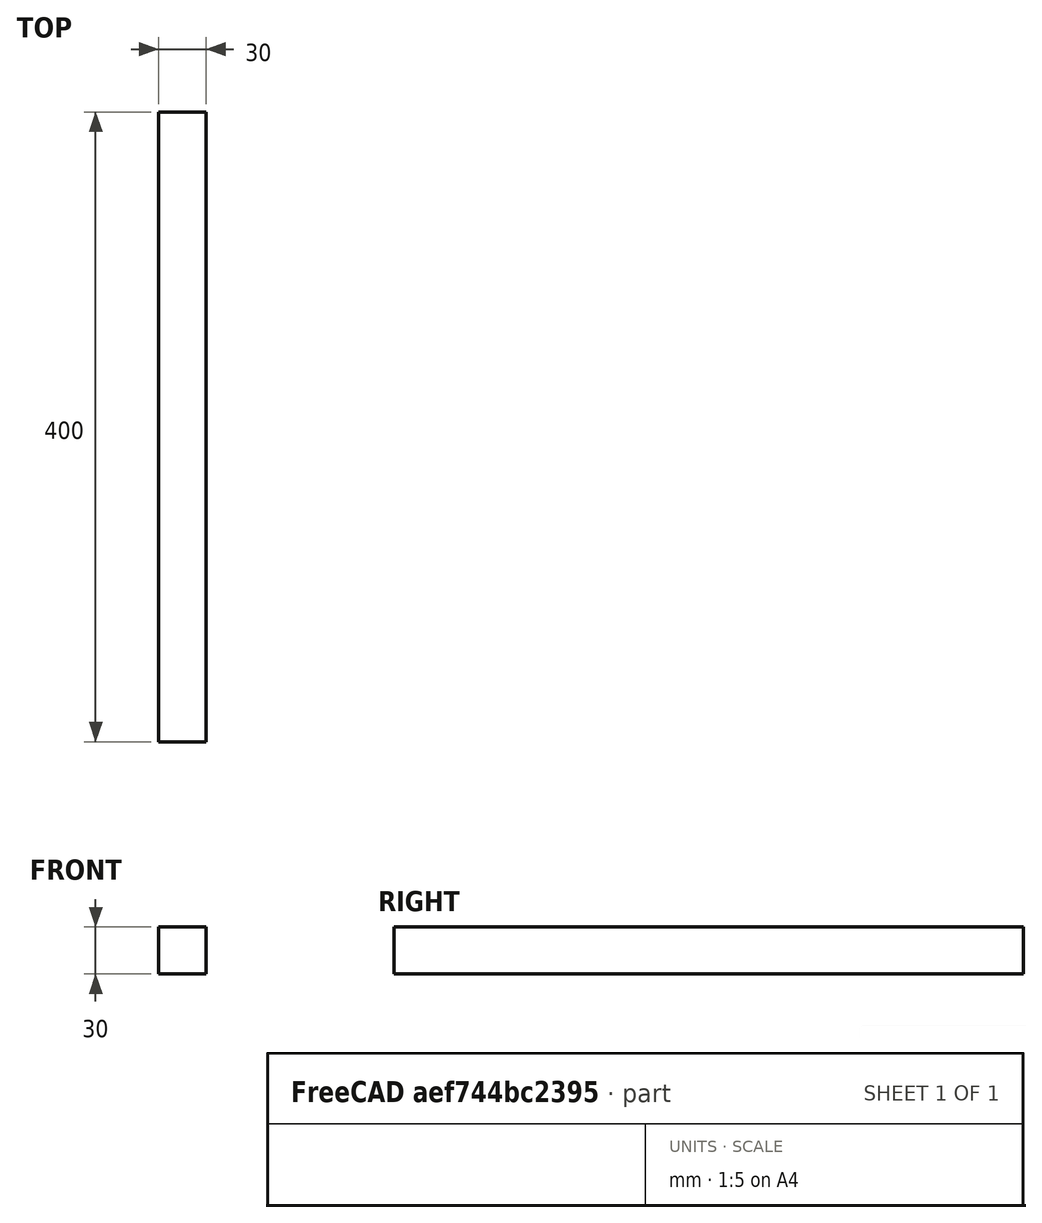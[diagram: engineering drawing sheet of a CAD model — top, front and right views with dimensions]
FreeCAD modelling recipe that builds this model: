
FCSTD DOCUMENT  (FreeCAD 0.20R29177 (Git))
Label: handlebarsides
License: All rights reserved
LicenseURL: http://en.wikipedia.org/wiki/All_rights_reserved
objects: Sketcher::SketchObject×1, PartDesign::Pad×1, PartDesign::Body×1
note: 4 computed .brp shape members not serialized (recipe doc carries the construction recipe); baked Part::Feature solids carry a one-line shape summary decoded from their .brp

FEATURE [Sketcher::SketchObject] Sketch
  FullyConstrained = true
  MapMode = 5
  Placement = pos=(0,0,0) rot=(1,0,0;1.5708rad)
  Support = -> [XZ_Plane]
  sketch-geometry (4):
    g0: LineSegment StartX=0 StartY=0 StartZ=0 EndX=30 EndY=0 EndZ=0
    g1: LineSegment StartX=30 StartY=0 StartZ=0 EndX=30 EndY=30 EndZ=0
    g2: LineSegment StartX=30 StartY=30 StartZ=0 EndX=0 EndY=30 EndZ=0
    g3: LineSegment StartX=0 StartY=30 StartZ=0 EndX=0 EndY=0 EndZ=0
  constraints (11):
    c: Coincident(g0,g1)
    c: Coincident(g1,g2)
    c: Coincident(g2,g3)
    c: Coincident(g3,g0)
    c: Horizontal(g0)
    c: Horizontal(g2)
    c: Vertical(g1)
    c: Vertical(g3)
    c: Coincident(g0,g-1)
    c: DistanceX(g2,g2) = 30
    c: DistanceY(g1,g1) = 30
FEATURE [PartDesign::Pad] Pad
  Direction = (1,1,1)
  Length = 400
  Length2 = 100
  Placement = pos=(0,0,0) rot=(1,0,0;1.5708rad)
  Profile = -> Sketch
  Type = 0
FEATURE [PartDesign::Body] Body  label="handlebarsides"
  Group = -> [Sketch,Pad]
  Origin = -> Origin
  Tip = -> Pad
